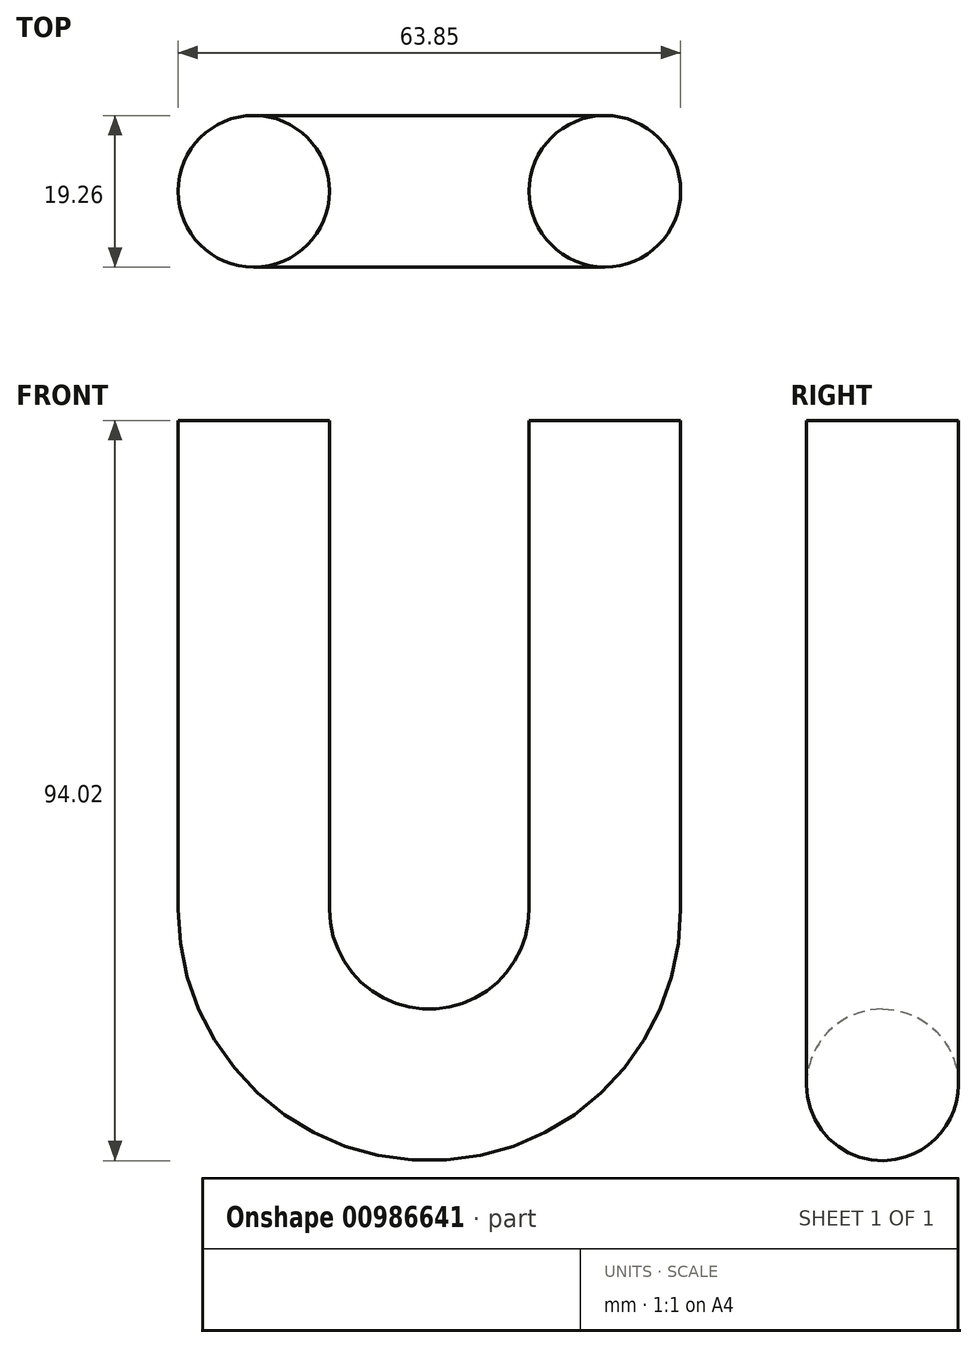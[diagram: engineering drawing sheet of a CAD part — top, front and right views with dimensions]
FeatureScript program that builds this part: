
annotation { "Feature Type Name" : "Feature", "Feature Type Description" : "" }
export const myFeature = defineFeature(function(context is Context, id is Id, definition is map)
    precondition{}
    {
        {
            var Q0;
            Q0=qCreatedBy(makeId("Front.planeOp"),FACE);
            var sketch = newSketch(context, id + "F0", { "sketchPlane" : qUnion([Q0])});
            skLineSegment(sketch, "E0", {"start": v(0, 0) * mm, "end": v(0, -62.1) * mm});
            skArc(sketch, "E1", {"start": v(0, -62.1) * mm, "mid": v(22.3, -84.39) * mm, "end": v(44.6, -62.1) * mm});
            skLineSegment(sketch, "E2", {"start": v(44.6, -62.1) * mm, "end": v(44.6, 0) * mm});
            skSolve(sketch);
        }
        {
            var Q0;
            Q0=qCreatedBy(makeId("Top.planeOp"),FACE);
            var sketch = newSketch(context, id + "F1", { "sketchPlane" : qUnion([Q0])});
            skCircle(sketch, "E3", {"center": v(0, 0) * mm, "radius": 9.63 * mm});
            skSolve(sketch);
        }
        {
            var Q0;
            Q0=makeQuery(id+"F1.imprint","IMPRINT",FACE,{"disambiguationData":[TD([[makeQuery(id+"F1.imprint","IMPRINT",EDGE,{"derivedFrom":sQuery(id+"F1.wireOp",EDGE,"E3")}),1.0]])]});
            var Q1;
            Q1=sQuery(id+"F0.wireOp",EDGE,"E0");
            var Q2;
            Q2=sQuery(id+"F0.wireOp",EDGE,"E1");
            var Q3;
            Q3=sQuery(id+"F0.wireOp",EDGE,"E2");
            sweep(context, id + "F2", {"profiles" : qUnion([Q0]), "path" : qUnion([Q1, Q2, Q3])});
        }
    });
